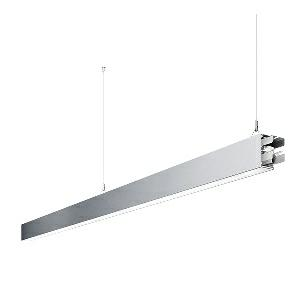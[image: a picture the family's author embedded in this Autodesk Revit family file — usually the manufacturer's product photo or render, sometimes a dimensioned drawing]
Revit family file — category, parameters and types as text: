
# Revit family: idoo_line_-_ilp_6000_vtl_d_mid_00806474_ab2e
name_source: partatom
category: Lighting Fixtures
units: mm (PartAtom-declared; Revit-internal decimal feet)

## family parameters
Cut with Voids When Loaded = No
Host = Face
Light Source = No
Part Type = Normal
Room Calculation Point = No
Round Connector Dimension = Use Diameter
Shared = No

## types (1)
- IDOO.line - ILP 6000/VTL/D MID (1 x LED, 6150 lm, 2700-6500K)
    Apparent Load = 63 VA
    Approval mark = CE
    CIE Flux Codes = 66 91 98 40 100
    Color Rendering = 90-100
    Color Temperature = 2700-6500K
    Control Gear = Electronic ballast
    Default Elevation = 1800 mm
    Description = ILP 6000/VTL/D|Suspended luminaire|light source: LED|connected load: 220-240 V, 50/60 Hz|Power consumption: approx. 63 W|standby: approx. 0,25|luminous flux: 6150 lm|luminous efficacy: 97 lm/W|light distribution: Direct/indirect|direct ratio: approx. 40 %|colour temperature: Cold white, ca. 2700-6500 K|color rendering index (CRI): >= 90|chromaticity tolerance:  3 SDCM|System of protection: IP 40|technology: Continuously dimmable|luminaire body|material: Sectional aluminium|colour: Silver|lamp cover: Acrylic (PMMA), Clear|mains lead: 1,0 m With free stranded wires|Fastening: Steel cable 0.3 - 0.7 m|glare control: Prism aperture|luminance(L65): <= 2700 cd/m|unified glare rating(4H 8H): <=  16|special features: Specified values at approx. 4000 K, DALI Load 1x, Through-wired, up to 18 m on one mains connection, External control required for Dali Device type 8, Flicker-free, Constant luminous flux between 2700 and 6500 K, Constant colour temperature over the whole dimming range, Suitable as emergency lighting, Mechanical and electrical connection of the individual modules without tools|
    Frequency = 50 Hz
    Height = 110 mm
    Lamp = 1 x LED
    Lamp Light Flux = 6150 lm
    Lamp count = 1
    Length = 2244 mm
    Luminous efficacy = 98 lm/W
    Manufacturer = Waldmann
    ModVariant = No
    Model = 00806474
    Mounting Place = Ceiling
    Mounting Type = Pendant
    Number of Poles = 1
    OnlyDefault = Yes
    Power Factor = 1
    Product Name = IDOO.line - ILP 6000/VTL/D MID
    Product group = Suspended luminaire
    ProductGroupID = 9
    Protection Class = Protection class I
    Protection Degree = IP 40
    RLX_Detail_Level = 1
    RLX_Emergency_Light_Flux = 0 lm
    RLX_Emergency_Type = 0
    RLX_Emergency_Type_DB = No
    RlxData = <blob elided: 24413 chars, md5=57e7926a>
    Socket = socket
    Standby Power = 0 W
    System Light Flux = 6150 lm
    System Power = 63 W
    Type Comments = Product without accessories
    Type Image = 113317000-00692618.jpg
    URL = http://relux.com
    VarID = ---
    Voltage = 230 V
    Voltage Range = 220-240 V
    Weight = 0.00 kg
    Width = 60 mm  [stored 0.19685 ft]

note: [stored X ft] marks values corroborated as IEEE doubles in the binary element streams (Revit-internal decimal feet)

## geometry (parser evidence)
native form markers: Blend x4, Sweep x14
no freeform markers — native parametric forms only
